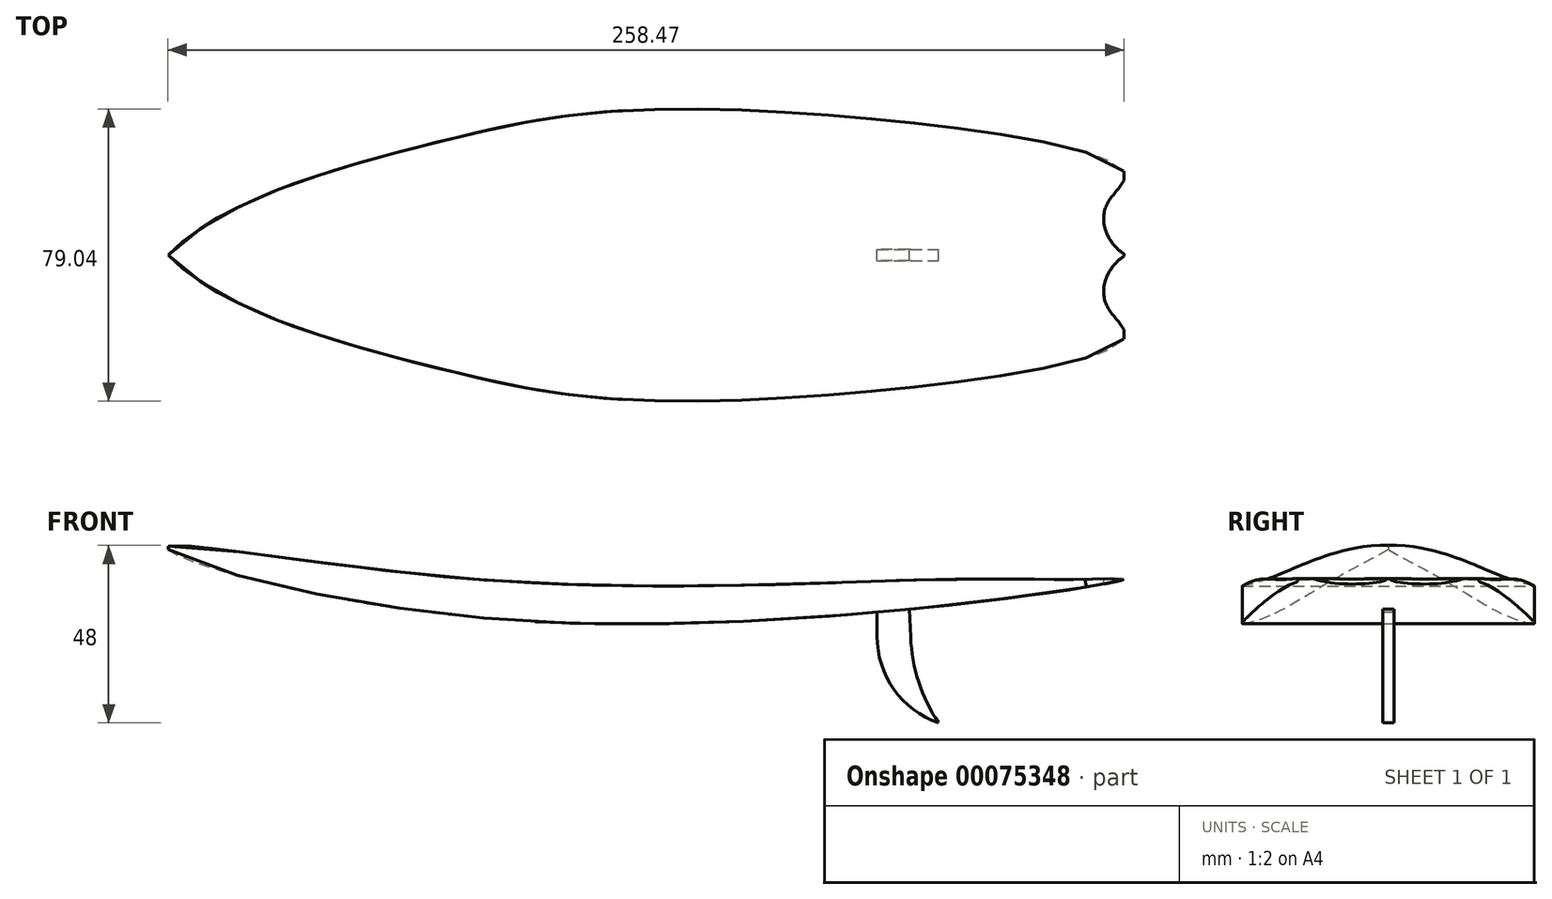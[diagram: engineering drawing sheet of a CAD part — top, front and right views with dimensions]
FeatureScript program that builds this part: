
annotation { "Feature Type Name" : "Feature", "Feature Type Description" : "" }
export const myFeature = defineFeature(function(context is Context, id is Id, definition is map)
    precondition{}
    {
        {
            var Q0;
            Q0=qCreatedBy(makeId("Front.planeOp"),FACE);
            var sketch = newSketch(context, id + "F0", { "sketchPlane" : qUnion([Q0])});
            skFitSpline(sketch, "E0", {"points": [v(-105.56, 8.76) * mm, v(-22.17, 0) * mm, v(105.84, 0) * mm, v(144.44, 0) * mm, v(153.14, 0) * mm, v(-9.76, -11.24) * mm, v(-105.56, 8.76) * mm]});
            skSolve(sketch);
        }
        {
            var Q0;
            Q0 = qSketchRegion(id + "F0", true);
            extrude(context, id + "F1", {"entities" : qUnion([Q0]), "endBound" : BoundingType.SYMMETRIC, "depth" : 100 * mm});
        }
        {
            var Q0;
            Q0=qCreatedBy(makeId("Top.planeOp"),FACE);
            var sketch = newSketch(context, id + "F2", { "sketchPlane" : qUnion([Q0])});
            skFitSpline(sketch, "E1", {"points": [v(-105.3, 0) * mm, v(-32.34, 30.58) * mm, v(43.95, 39.4) * mm, v(153.3, 22.36) * mm, v(148.3, 13.06) * mm, v(153.66, 0) * mm], "startDerivative": vector(170.58, 180.81) * mm, "endDerivative": vector(133.82, -80.12) * mm});
            skLineSegment(sketch, "E2", {"start": v(153.66, 0) * mm, "end": v(-105.3, 0) * mm, "construction": true});
            skFitSpline(sketch, "E3.MirrorCS", {"points": [v(-105.3, 0) * mm, v(-32.34, -30.58) * mm, v(43.95, -39.4) * mm, v(153.3, -22.36) * mm, v(148.3, -13.06) * mm, v(153.66, 0) * mm], "startDerivative": vector(170.58, -180.81) * mm, "endDerivative": vector(133.82, 80.12) * mm});
            skSolve(sketch);
        }
        {
            var Q0;
            Q0 = qSketchRegion(id + "F2", true);
            extrude(context, id + "F3", {"entities" : qUnion([Q0]), "operationType" : NewBodyOperationType.INTERSECT, "endBound" : BoundingType.SYMMETRIC, "depth" : 800 * mm});
        }
        {
            var Q0;
            Q0=qCreatedBy(makeId("Front.planeOp"),FACE);
            var sketch = newSketch(context, id + "F4", { "sketchPlane" : qUnion([Q0])});
            skLineSegment(sketch, "E4", {"start": v(86.42, -7.47) * mm, "end": v(86.42, -15.43) * mm});
            skArc(sketch, "E5", {"start": v(86.42, -15.43) * mm, "mid": v(91, -29.8) * mm, "end": v(103.08, -38.84) * mm});
            skArc(sketch, "E6", {"start": v(95.5, -15.73) * mm, "mid": v(97.7, -27.8) * mm, "end": v(103.08, -38.84) * mm});
            skLineSegment(sketch, "E7", {"start": v(95.5, -15.73) * mm, "end": v(95.1, -6.92) * mm});
            skLineSegment(sketch, "E8", {"start": v(95.1, -6.92) * mm, "end": v(86.42, -7.47) * mm});
            skSolve(sketch);
        }
        {
            var Q0;
            Q0=makeQuery(id+"F4.imprint","IMPRINT",FACE,{"disambiguationData":[TD([[makeQuery(id+"F4.imprint","IMPRINT",EDGE,{"derivedFrom":sQuery(id+"F4.wireOp",EDGE,"E4")}),1.0]])]});
            extrude(context, id + "F5", {"entities" : qUnion([Q0]), "operationType" : NewBodyOperationType.ADD, "endBound" : BoundingType.SYMMETRIC, "depth" : 3 * mm});
        }
    });
